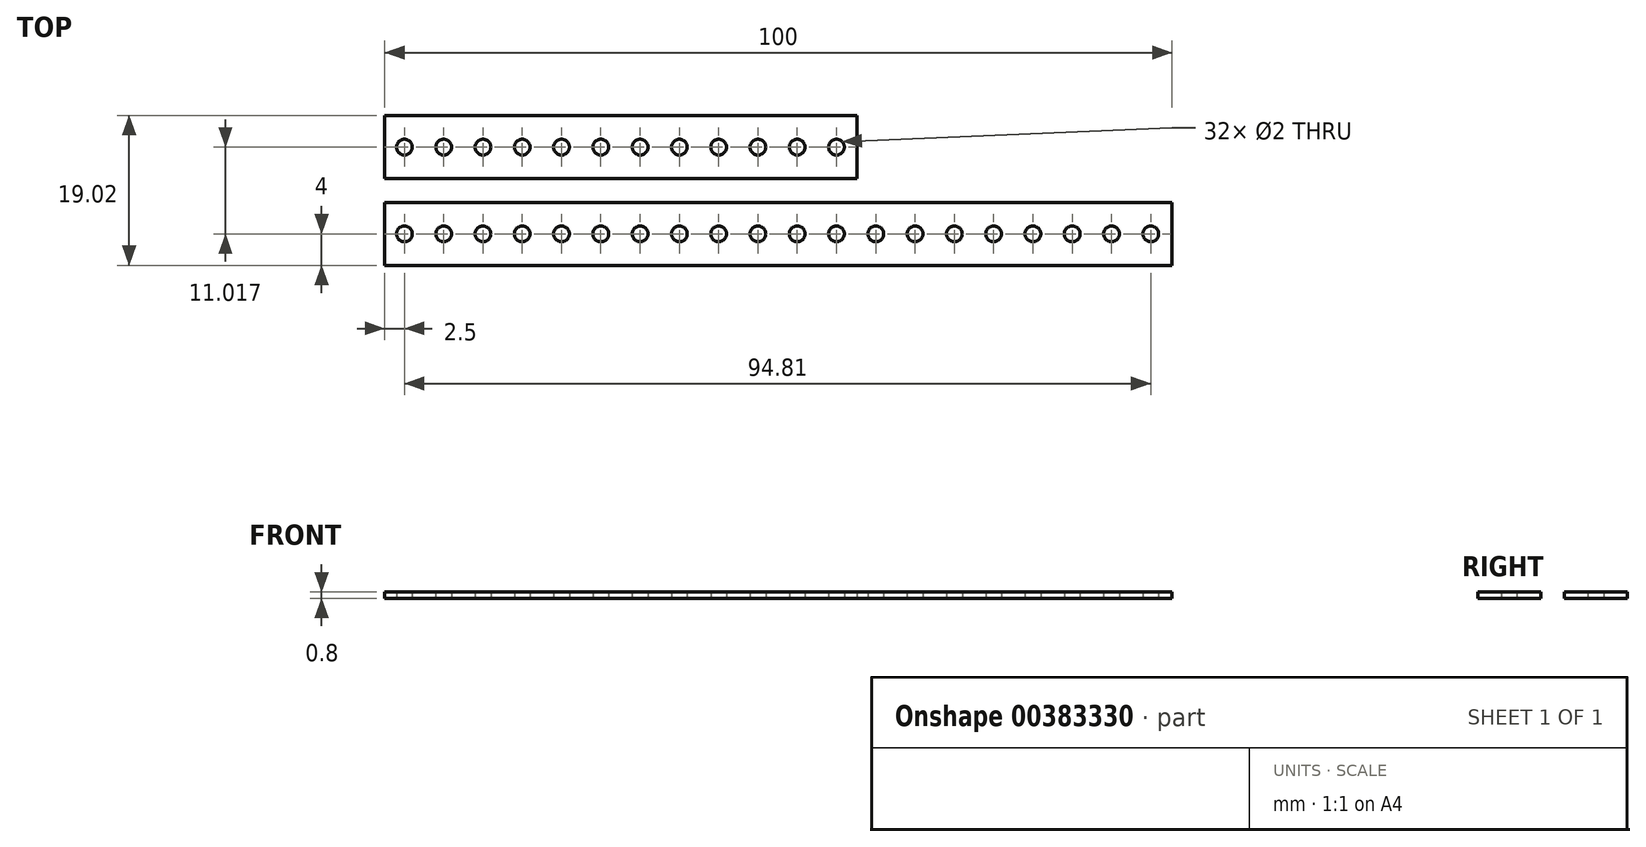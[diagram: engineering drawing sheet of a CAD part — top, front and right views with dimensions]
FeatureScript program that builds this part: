
annotation { "Feature Type Name" : "Feature", "Feature Type Description" : "" }
export const myFeature = defineFeature(function(context is Context, id is Id, definition is map)
    precondition{}
    {
        {
            var Q0;
            Q0=qCreatedBy(makeId("Top.planeOp"),FACE);
            var sketch = newSketch(context, id + "F0", { "sketchPlane" : qUnion([Q0])});
            skLineSegment(sketch, "E0.bottom", {"start": v(0, 0) * mm, "end": v(100, 0) * mm});
            skLineSegment(sketch, "E0.top", {"start": v(0, -8) * mm, "end": v(100, -8) * mm});
            skLineSegment(sketch, "E0.left", {"start": v(0, 0) * mm, "end": v(0, -8) * mm});
            skLineSegment(sketch, "E0.right", {"start": v(100, 0) * mm, "end": v(100, -8) * mm});
            skLineSegment(sketch, "E1.bottom", {"start": v(0, 0) * mm, "end": v(60, 0) * mm});
            skLineSegment(sketch, "E1.top", {"start": v(0, 11.02) * mm, "end": v(60, 11.02) * mm});
            skLineSegment(sketch, "E2", {"start": v(0, 3.02) * mm, "end": v(60, 3.02) * mm});
            skLineSegment(sketch, "E3", {"start": v(0, 11.02) * mm, "end": v(0, 3.02) * mm});
            skLineSegment(sketch, "E4", {"start": v(60, 11.02) * mm, "end": v(60, 3.02) * mm});
            skLineSegment(sketch, "E5", {"start": v(0, 7.02) * mm, "end": v(60, 7.02) * mm});
            skLineSegment(sketch, "E6", {"start": v(0, -4) * mm, "end": v(100, -4) * mm});
            skPoint(sketch, "E7", {"position": v(2.5, -4) * mm});
            skCircle(sketch, "E8", {"center": v(2.5, -4) * mm, "radius": 1 * mm});
            skCircle(sketch, "E9.1.0.0", {"center": v(7.5, -4) * mm, "radius": 1 * mm});
            skCircle(sketch, "E9.2.0.0", {"center": v(12.48, -4) * mm, "radius": 1 * mm});
            skCircle(sketch, "E9.3.0.0", {"center": v(17.47, -4) * mm, "radius": 1 * mm});
            skCircle(sketch, "E9.4.0.0", {"center": v(22.46, -4) * mm, "radius": 1 * mm});
            skCircle(sketch, "E9.5.0.0", {"center": v(27.45, -4) * mm, "radius": 1 * mm});
            skCircle(sketch, "E9.6.0.0", {"center": v(32.44, -4) * mm, "radius": 1 * mm});
            skCircle(sketch, "E9.7.0.0", {"center": v(37.43, -4) * mm, "radius": 1 * mm});
            skCircle(sketch, "E9.8.0.0", {"center": v(42.42, -4) * mm, "radius": 1 * mm});
            skCircle(sketch, "E9.9.0.0", {"center": v(47.41, -4) * mm, "radius": 1 * mm});
            skCircle(sketch, "E9.10.0.0", {"center": v(52.4, -4) * mm, "radius": 1 * mm});
            skCircle(sketch, "E9.11.0.0", {"center": v(57.39, -4) * mm, "radius": 1 * mm});
            skCircle(sketch, "E9.12.0.0", {"center": v(62.38, -4) * mm, "radius": 1 * mm});
            skCircle(sketch, "E9.13.0.0", {"center": v(67.37, -4) * mm, "radius": 1 * mm});
            skCircle(sketch, "E9.14.0.0", {"center": v(72.36, -4) * mm, "radius": 1 * mm});
            skCircle(sketch, "E9.15.0.0", {"center": v(77.35, -4) * mm, "radius": 1 * mm});
            skCircle(sketch, "E9.16.0.0", {"center": v(82.34, -4) * mm, "radius": 1 * mm});
            skCircle(sketch, "E9.17.0.0", {"center": v(87.33, -4) * mm, "radius": 1 * mm});
            skCircle(sketch, "E9.18.0.0", {"center": v(92.32, -4) * mm, "radius": 1 * mm});
            skCircle(sketch, "E9.19.0.0", {"center": v(97.3, -4) * mm, "radius": 1 * mm});
            skLineSegment(sketch, "E9.direction1", {"start": v(2.5, -4) * mm, "end": v(7.5, -4) * mm, "construction": true});
            skPoint(sketch, "E10", {"position": v(2.5, 7.02) * mm});
            skCircle(sketch, "E11", {"center": v(2.5, 7.02) * mm, "radius": 1 * mm});
            skCircle(sketch, "E12.1.0.0", {"center": v(7.5, 7.02) * mm, "radius": 1 * mm});
            skCircle(sketch, "E12.2.0.0", {"center": v(12.48, 7.02) * mm, "radius": 1 * mm});
            skCircle(sketch, "E12.3.0.0", {"center": v(17.47, 7.02) * mm, "radius": 1 * mm});
            skCircle(sketch, "E12.4.0.0", {"center": v(22.46, 7.02) * mm, "radius": 1 * mm});
            skCircle(sketch, "E12.5.0.0", {"center": v(27.45, 7.02) * mm, "radius": 1 * mm});
            skCircle(sketch, "E12.6.0.0", {"center": v(32.44, 7.02) * mm, "radius": 1 * mm});
            skCircle(sketch, "E12.7.0.0", {"center": v(37.43, 7.02) * mm, "radius": 1 * mm});
            skCircle(sketch, "E12.8.0.0", {"center": v(42.42, 7.02) * mm, "radius": 1 * mm});
            skCircle(sketch, "E12.9.0.0", {"center": v(47.41, 7.02) * mm, "radius": 1 * mm});
            skCircle(sketch, "E12.10.0.0", {"center": v(52.4, 7.02) * mm, "radius": 1 * mm});
            skCircle(sketch, "E12.11.0.0", {"center": v(57.4, 7.02) * mm, "radius": 1 * mm});
            skLineSegment(sketch, "E12.direction1", {"start": v(2.5, 7.02) * mm, "end": v(7.5, 7.02) * mm, "construction": true});
            skSolve(sketch);
        }
        {
            var Q0;
            {var subQ41=sQuery(id+"F0.wireOp",EDGE,"E1.top");Q0=makeQuery(id+"F0.imprint","IMPRINT",FACE,{"disambiguationData":[TD([[makeQuery(id+"F0.imprint","IMPRINT",EDGE,{"derivedFrom":subQ41}),-1.0]])]});}
            var Q1;
            {var subQ27=sQuery(id+"F0.wireOp",EDGE,"E2");Q1=makeQuery(id+"F0.imprint","IMPRINT",FACE,{"disambiguationData":[TD([[makeQuery(id+"F0.imprint","IMPRINT",EDGE,{"derivedFrom":subQ27}),1.0]])]});}
            var Q2;
            {var subQ47=sQuery(id+"F0.wireOp",EDGE,"E0.bottom");Q2=makeQuery(id+"F0.imprint","IMPRINT",FACE,{"disambiguationData":[TD([[makeQuery(id+"F0.imprint","IMPRINT",EDGE,{"derivedFrom":subQ47}),-1.0]])]});}
            var Q3;
            {var subQ30=sQuery(id+"F0.wireOp",EDGE,"E0.top");Q3=makeQuery(id+"F0.imprint","IMPRINT",FACE,{"disambiguationData":[TD([[makeQuery(id+"F0.imprint","IMPRINT",EDGE,{"derivedFrom":subQ30}),1.0]])]});}
            extrude(context, id + "F1", {"entities" : qUnion([Q0, Q1, Q2, Q3]), "depth" : 0.8 * mm});
        }
    });
